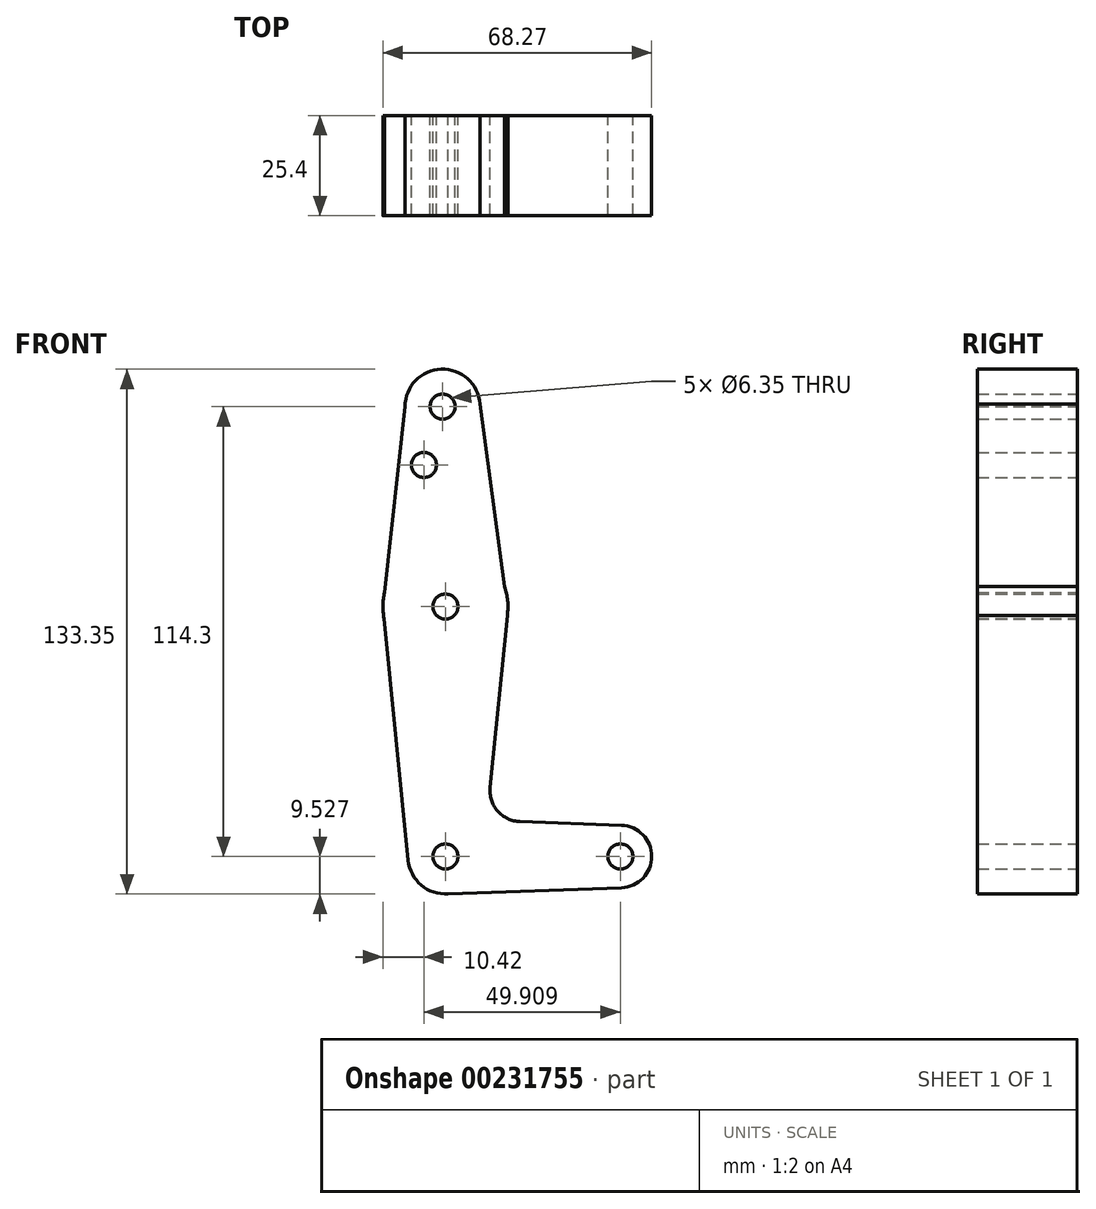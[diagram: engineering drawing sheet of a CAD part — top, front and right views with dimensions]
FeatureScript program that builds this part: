
annotation { "Feature Type Name" : "Feature", "Feature Type Description" : "" }
export const myFeature = defineFeature(function(context is Context, id is Id, definition is map)
    precondition{}
    {
        {
            var Q0;
            Q0=qCreatedBy(makeId("Front.planeOp"),FACE);
            var sketch = newSketch(context, id + "F0", { "sketchPlane" : qUnion([Q0])});
            skLineSegment(sketch, "E0", {"start": v(-12.3, 59.97) * mm, "end": v(-11.58, 9.17) * mm});
            skLineSegment(sketch, "E1", {"start": v(-11.58, 9.17) * mm, "end": v(-11.58, -54.33) * mm});
            skLineSegment(sketch, "E2", {"start": v(-11.58, -54.33) * mm, "end": v(32.87, -54.33) * mm});
            skCircle(sketch, "E3", {"center": v(-12.3, 59.97) * mm, "radius": 9.53 * mm});
            skCircle(sketch, "E4", {"center": v(-11.58, 9.17) * mm, "radius": 15.88 * mm});
            skCircle(sketch, "E5", {"center": v(-11.58, -54.33) * mm, "radius": 9.53 * mm});
            skCircle(sketch, "E6", {"center": v(32.87, -54.33) * mm, "radius": 7.94 * mm});
            skLineSegment(sketch, "E7", {"start": v(-21.83, 59.97) * mm, "end": v(-27.46, 9.06) * mm});
            skLineSegment(sketch, "E8", {"start": v(-27.46, 9.06) * mm, "end": v(-21.06, -55.27) * mm});
            skLineSegment(sketch, "E9", {"start": v(-2.8, 60.66) * mm, "end": v(4.27, 8.23) * mm});
            skLineSegment(sketch, "E10", {"start": v(4.27, 8.23) * mm, "end": v(-0.24, -36.74) * mm});
            skLineSegment(sketch, "E11", {"start": v(7.38, -45.48) * mm, "end": v(33.15, -46.4) * mm});
            skLineSegment(sketch, "E12", {"start": v(-11.58, -63.86) * mm, "end": v(33.15, -62.26) * mm});
            skCircle(sketch, "E13", {"center": v(-17.04, 45.15) * mm, "radius": 3.18 * mm});
            skPoint(sketch, "E14.newPointB", {"position": v(-11.58, -44.8) * mm});
            skArc(sketch, "E14.filletArc", {"start": v(-0.24, -36.74) * mm, "mid": v(1.68, -42.77) * mm, "end": v(7.38, -45.48) * mm});
            skCircle(sketch, "E15", {"center": v(-12.3, 59.97) * mm, "radius": 3.18 * mm});
            skCircle(sketch, "E16", {"center": v(-11.58, 9.17) * mm, "radius": 3.18 * mm});
            skCircle(sketch, "E17", {"center": v(-11.58, -54.33) * mm, "radius": 3.18 * mm});
            skCircle(sketch, "E18", {"center": v(32.87, -54.33) * mm, "radius": 3.18 * mm});
            skSolve(sketch);
        }
        {
            var Q0;
            Q0 = qSketchRegion(id + "F0", true);
            extrude(context, id + "F1", {"entities" : qUnion([Q0]), "depth" : 25.4 * mm});
        }
        {
            var Q0;
            {var subQ0=sQuery(id+"F0.wireOp",EDGE,"E5");var subQ1=sQuery(id+"F0.wireOp",EDGE,"E1");var subQ2=makeQuery(id+"F0.imprint","INTERSECT",VERTEX,{"derivedFrom":[subQ1,subQ0]});Q0=makeQuery(id+"F0.imprint","IMPRINT",FACE,{"disambiguationData":[TD([[makeQuery(id+"F0.imprint","IMPRINT",EDGE,{"disambiguationData":[TD([[subQ2,-1.0]])],"derivedFrom":subQ1}),1.0]])]});}
            extrude(context, id + "F2", {"entities" : qUnion([Q0]), "operationType" : NewBodyOperationType.ADD, "depth" : 25.4 * mm});
        }
    });
